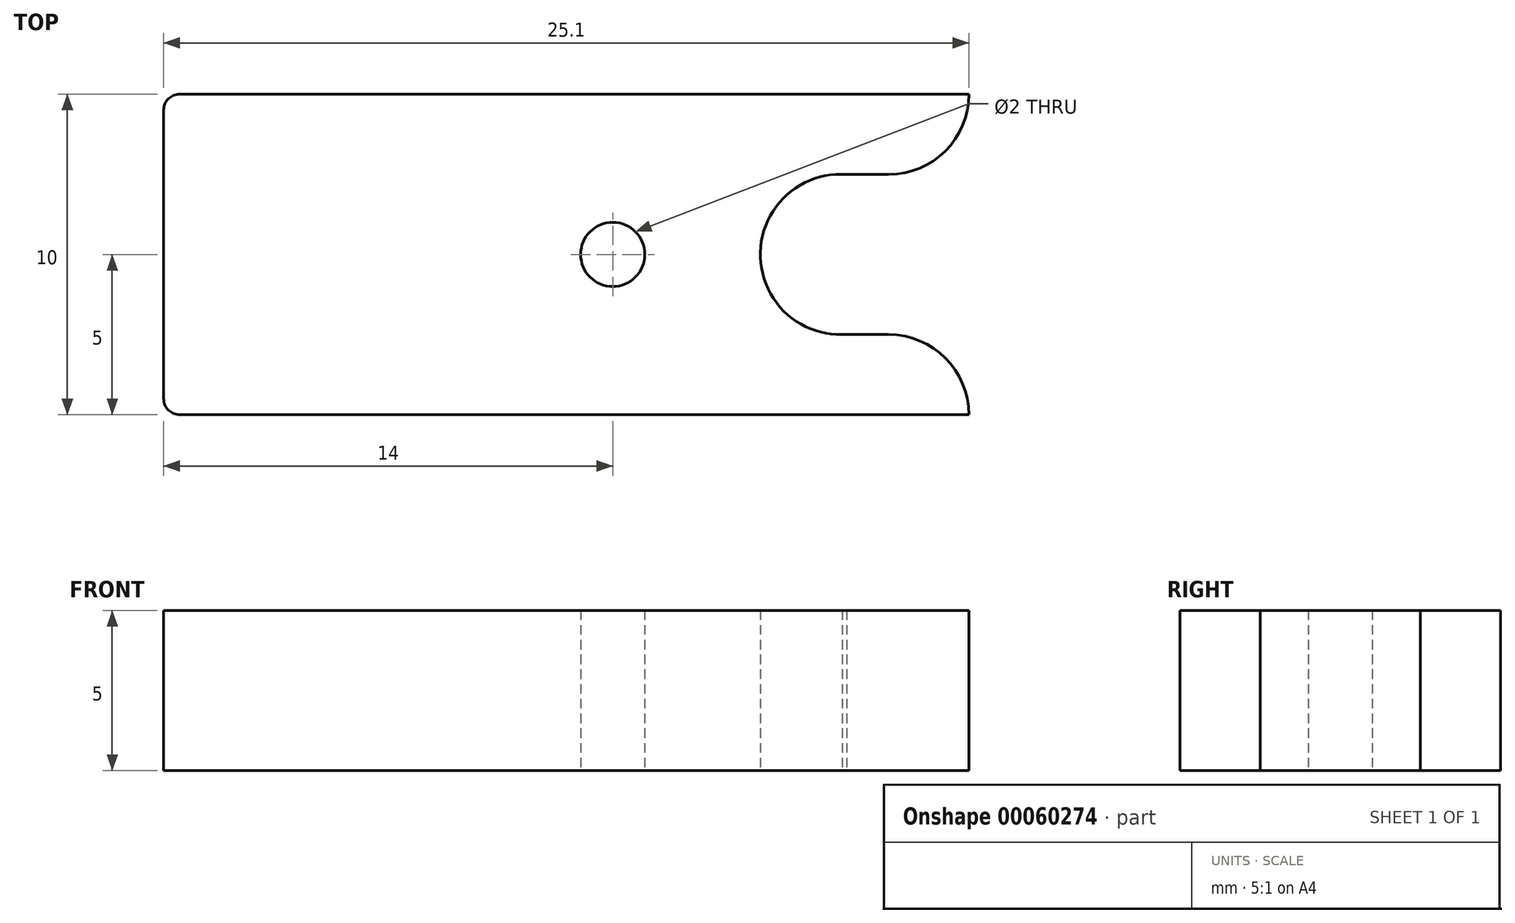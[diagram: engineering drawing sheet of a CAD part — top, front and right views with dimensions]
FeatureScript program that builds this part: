
annotation { "Feature Type Name" : "Feature", "Feature Type Description" : "" }
export const myFeature = defineFeature(function(context is Context, id is Id, definition is map)
    precondition{}
    {
        {
            var Q0;
            Q0=qCreatedBy(makeId("Top.planeOp"),FACE);
            var sketch = newSketch(context, id + "F0", { "sketchPlane" : qUnion([Q0])});
            skLineSegment(sketch, "E0.bottom", {"start": v(0.5, 0) * mm, "end": v(25.1, 0) * mm});
            skLineSegment(sketch, "E0.top", {"start": v(0.5, -10) * mm, "end": v(25.1, -10) * mm});
            skLineSegment(sketch, "E0.left", {"start": v(0, -0.5) * mm, "end": v(0, -9.5) * mm});
            skLineSegment(sketch, "E1", {"start": v(0, -5) * mm, "end": v(25.1, -5) * mm, "construction": true});
            skCircle(sketch, "E2", {"center": v(14, -5) * mm, "radius": 1 * mm});
            skArc(sketch, "E3", {"start": v(21.3, -2.5) * mm, "mid": v(18.6, -4.93) * mm, "end": v(21.15, -7.5) * mm});
            skLineSegment(sketch, "E4", {"start": v(21.15, -7.5) * mm, "end": v(22.6, -7.5) * mm});
            skLineSegment(sketch, "E5", {"start": v(20.9, -2.5) * mm, "end": v(22.6, -2.5) * mm});
            skLineSegment(sketch, "E6", {"start": v(25.1, -10) * mm, "end": v(25.1, -10) * mm});
            skLineSegment(sketch, "E7", {"start": v(25.1, 0) * mm, "end": v(25.1, 0) * mm});
            skArc(sketch, "E8.filletArc", {"start": v(25.1, -10) * mm, "mid": v(24.37, -8.23) * mm, "end": v(22.6, -7.5) * mm});
            skArc(sketch, "E9.filletArc", {"start": v(22.6, -2.5) * mm, "mid": v(24.37, -1.78) * mm, "end": v(25.1, 0) * mm});
            skPoint(sketch, "E10.visualSharp", {"position": v(0, 0) * mm});
            skArc(sketch, "E10.filletArc", {"start": v(0.5, 0) * mm, "mid": v(0.15, -0.15) * mm, "end": v(0, -0.5) * mm});
            skPoint(sketch, "E11.visualSharp", {"position": v(0, -10) * mm});
            skArc(sketch, "E11.filletArc", {"start": v(0, -9.5) * mm, "mid": v(0.15, -9.85) * mm, "end": v(0.5, -10) * mm});
            skSolve(sketch);
        }
        {
            var Q0;
            Q0=makeQuery(id+"F0.imprint","IMPRINT",FACE,{"disambiguationData":[TD([[makeQuery(id+"F0.imprint","IMPRINT",EDGE,{"derivedFrom":sQuery(id+"F0.wireOp",EDGE,"E0.bottom")}),-1.0]])]});
            extrude(context, id + "F1", {"entities" : qUnion([Q0]), "depth" : 5 * mm});
        }
    });
